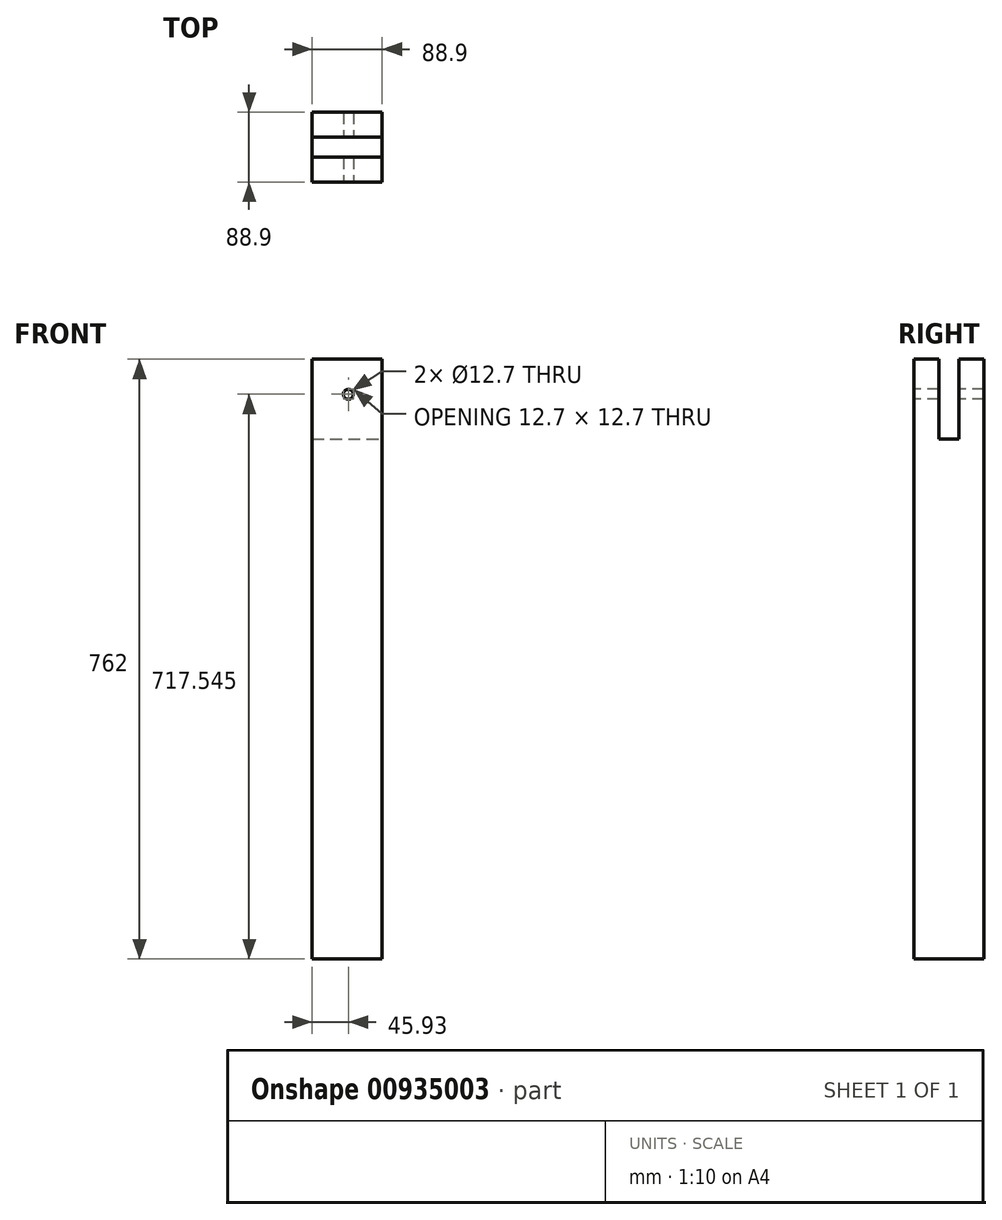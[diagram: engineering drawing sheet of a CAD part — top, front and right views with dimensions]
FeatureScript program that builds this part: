
annotation { "Feature Type Name" : "Feature", "Feature Type Description" : "" }
export const myFeature = defineFeature(function(context is Context, id is Id, definition is map)
    precondition{}
    {
        {
            var Q0;
            Q0=qCreatedBy(makeId("Front.planeOp"),FACE);
            var sketch = newSketch(context, id + "F0", { "sketchPlane" : qUnion([Q0])});
            skLineSegment(sketch, "E0.bottom", {"start": v(-45.93, 708.32) * mm, "end": v(42.97, 708.32) * mm});
            skLineSegment(sketch, "E0.top", {"start": v(-45.93, -53.68) * mm, "end": v(42.97, -53.68) * mm});
            skLineSegment(sketch, "E0.left", {"start": v(-45.93, 708.32) * mm, "end": v(-45.93, -53.68) * mm});
            skLineSegment(sketch, "E0.right", {"start": v(42.97, 708.32) * mm, "end": v(42.97, -53.68) * mm});
            skSolve(sketch);
        }
        {
            var Q0;
            Q0 = qSketchRegion(id + "F0", true);
            extrude(context, id + "F1", {"entities" : qUnion([Q0]), "depth" : 88.9 * mm, "offsetDistance" : 25.4 * mm, "symmetric" : true});
        }
        {
            var Q0;
            Q0=qCreatedBy(makeId("Right.planeOp"),FACE);
            var sketch = newSketch(context, id + "F2", { "sketchPlane" : qUnion([Q0])});
            skLineSegment(sketch, "E1.bottom", {"start": v(12.7, 606.72) * mm, "end": v(-12.7, 606.72) * mm});
            skLineSegment(sketch, "E1.top", {"start": v(12.7, 708.32) * mm, "end": v(-12.7, 708.32) * mm});
            skLineSegment(sketch, "E1.left", {"start": v(12.7, 606.72) * mm, "end": v(12.7, 708.32) * mm});
            skLineSegment(sketch, "E1.right", {"start": v(-12.7, 606.72) * mm, "end": v(-12.7, 708.32) * mm});
            skPoint(sketch, "E1.middle", {"position": v(0, 657.52) * mm});
            skSolve(sketch);
        }
        {
            var Q0;
            Q0 = qSketchRegion(id + "F2", true);
            extrude(context, id + "F3", {"entities" : qUnion([Q0]), "operationType" : NewBodyOperationType.REMOVE, "oppositeDirection" : true, "depth" : 254 * mm, "offsetDistance" : 25.4 * mm, "symmetric" : true});
        }
        {
            var Q0;
            Q0=makeQuery(id+"F1.opExtrude","CAP_FACE",FACE,{"disambiguationData":[OSD([sQuery(id+"F0.wireOp",EDGE,"E0.bottom"),sQuery(id+"F0.wireOp",EDGE,"E0.top"),sQuery(id+"F0.wireOp",EDGE,"E0.left"),sQuery(id+"F0.wireOp",EDGE,"E0.right")])],"isStart":true});
            var sketch = newSketch(context, id + "F4", { "sketchPlane" : qUnion([Q0])});
            skCircle(sketch, "E2", {"center": v(0, 663.87) * mm, "radius": 6.35 * mm});
            skSolve(sketch);
        }
        {
            var Q0;
            Q0 = qSketchRegion(id + "F4", true);
            extrude(context, id + "F5", {"entities" : qUnion([Q0]), "operationType" : NewBodyOperationType.REMOVE, "depth" : 254 * mm, "offsetDistance" : 25.4 * mm, "symmetric" : true});
        }
    });
